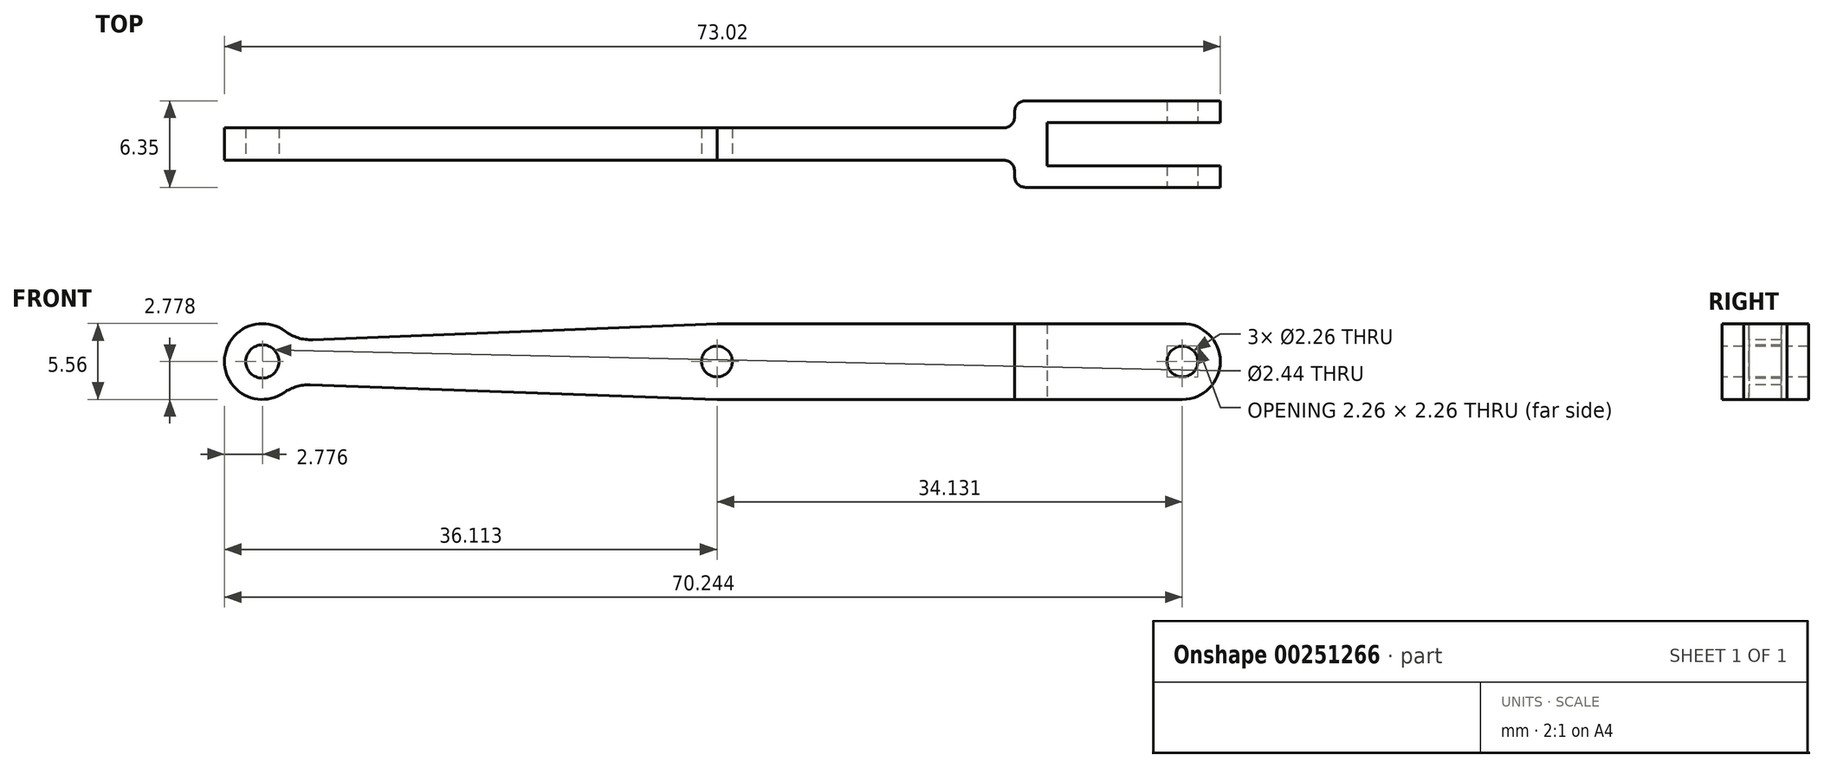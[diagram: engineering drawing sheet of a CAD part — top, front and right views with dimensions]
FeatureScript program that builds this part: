
annotation { "Feature Type Name" : "Feature", "Feature Type Description" : "" }
export const myFeature = defineFeature(function(context is Context, id is Id, definition is map)
    precondition{}
    {
        {
            var Q0;
            Q0=qCreatedBy(makeId("Top.planeOp"),FACE);
            var sketch = newSketch(context, id + "F0", { "sketchPlane" : qUnion([Q0])});
            skLineSegment(sketch, "E0", {"start": v(-28.05, 23.01) * mm, "end": v(29.1, 23.01) * mm});
            skLineSegment(sketch, "E1", {"start": v(29.9, 23.8) * mm, "end": v(29.9, 24.2) * mm});
            skLineSegment(sketch, "E2", {"start": v(30.68, 25) * mm, "end": v(44.97, 25) * mm});
            skLineSegment(sketch, "E3", {"start": v(44.97, 25) * mm, "end": v(44.97, 23.4) * mm});
            skLineSegment(sketch, "E4", {"start": v(44.97, 23.4) * mm, "end": v(32.27, 23.4) * mm});
            skLineSegment(sketch, "E5", {"start": v(32.27, 23.4) * mm, "end": v(32.27, 20.23) * mm});
            skLineSegment(sketch, "E6", {"start": v(32.27, 20.23) * mm, "end": v(44.97, 20.23) * mm});
            skLineSegment(sketch, "E7", {"start": v(44.97, 20.23) * mm, "end": v(44.97, 18.65) * mm});
            skLineSegment(sketch, "E8", {"start": v(44.97, 18.65) * mm, "end": v(30.68, 18.65) * mm});
            skLineSegment(sketch, "E9", {"start": v(29.9, 19.44) * mm, "end": v(29.9, 19.84) * mm});
            skLineSegment(sketch, "E10", {"start": v(29.1, 20.63) * mm, "end": v(-28.05, 20.63) * mm});
            skLineSegment(sketch, "E11", {"start": v(-28.05, 20.63) * mm, "end": v(-28.05, 23.01) * mm});
            skPoint(sketch, "E12.visualSharp", {"position": v(29.9, 23.01) * mm});
            skArc(sketch, "E12.filletArc", {"start": v(29.1, 23.01) * mm, "mid": v(29.66, 23.25) * mm, "end": v(29.9, 23.8) * mm});
            skPoint(sketch, "E13.visualSharp", {"position": v(29.9, 25) * mm});
            skArc(sketch, "E13.filletArc", {"start": v(30.68, 25) * mm, "mid": v(30.12, 24.76) * mm, "end": v(29.9, 24.2) * mm});
            skPoint(sketch, "E14.visualSharp", {"position": v(29.9, 20.63) * mm});
            skArc(sketch, "E14.filletArc", {"start": v(29.9, 19.84) * mm, "mid": v(29.66, 20.4) * mm, "end": v(29.1, 20.63) * mm});
            skPoint(sketch, "E15.visualSharp", {"position": v(29.9, 18.65) * mm});
            skArc(sketch, "E15.filletArc", {"start": v(29.9, 19.44) * mm, "mid": v(30.12, 18.88) * mm, "end": v(30.68, 18.65) * mm});
            skSolve(sketch);
        }
        {
            var Q0;
            Q0 = qSketchRegion(id + "F0", true);
            extrude(context, id + "F1", {"entities" : qUnion([Q0]), "depth" : 5.56 * mm});
        }
        {
            var Q0;
            Q0=makeQuery(id+"F1.opExtrude","SWEPT_FACE",FACE,{"disambiguationData":[OSD([sQuery(id+"F0.wireOp",EDGE,"E10")])]});
            var sketch = newSketch(context, id + "F2", { "sketchPlane" : qUnion([Q0])});
            skCircle(sketch, "E16", {"center": v(-25.27, 2.78) * mm, "radius": 1.22 * mm});
            skSolve(sketch);
        }
        {
            var Q0;
            Q0 = qSketchRegion(id + "F2", true);
            extrude(context, id + "F3", {"entities" : qUnion([Q0]), "operationType" : NewBodyOperationType.REMOVE, "oppositeDirection" : true, "depth" : 25.4 * mm});
        }
        {
            var Q0;
            Q0=makeQuery(id+"F1.opExtrude","SWEPT_FACE",FACE,{"disambiguationData":[OSD([sQuery(id+"F0.wireOp",EDGE,"E8")])]});
            var sketch = newSketch(context, id + "F4", { "sketchPlane" : qUnion([Q0])});
            skCircle(sketch, "E17", {"center": v(42.2, 2.78) * mm, "radius": 1.13 * mm});
            skSolve(sketch);
        }
        {
            var Q0;
            Q0 = qSketchRegion(id + "F4", true);
            extrude(context, id + "F5", {"entities" : qUnion([Q0]), "operationType" : NewBodyOperationType.REMOVE, "oppositeDirection" : true, "depth" : 25.4 * mm});
        }
        {
            var Q0;
            Q0=makeQuery(id+"F1.opExtrude","CAP_EDGE",EDGE,{"disambiguationData":[OSD([sQuery(id+"F0.wireOp",EDGE,"E7")])],"isStart":false});
            var Q1;
            Q1=makeQuery(id+"F1.opExtrude","CAP_EDGE",EDGE,{"disambiguationData":[OSD([sQuery(id+"F0.wireOp",EDGE,"E7")])],"isStart":true});
            var Q2;
            Q2=makeQuery(id+"F1.opExtrude","CAP_EDGE",EDGE,{"disambiguationData":[OSD([sQuery(id+"F0.wireOp",EDGE,"E3")])],"isStart":true});
            var Q3;
            Q3=makeQuery(id+"F1.opExtrude","CAP_EDGE",EDGE,{"disambiguationData":[OSD([sQuery(id+"F0.wireOp",EDGE,"E3")])],"isStart":false});
            fillet(context, id + "F6", {"entities" : qUnion([Q0, Q1, Q2, Q3]), "radius" : 2.78 * mm, "tangentPropagation" : true, "allowEdgeOverflow" : false});
        }
        {
            var Q0;
            Q0=makeQuery(id+"F1.opExtrude","CAP_EDGE",EDGE,{"disambiguationData":[OSD([sQuery(id+"F0.wireOp",EDGE,"E11")])],"isStart":false});
            var Q1;
            Q1=makeQuery(id+"F1.opExtrude","CAP_EDGE",EDGE,{"disambiguationData":[OSD([sQuery(id+"F0.wireOp",EDGE,"E11")])],"isStart":true});
            fillet(context, id + "F7", {"entities" : qUnion([Q0, Q1]), "radius" : 2.78 * mm, "tangentPropagation" : true, "allowEdgeOverflow" : false});
        }
        {
            var Q0;
            Q0=makeQuery(id+"F1.opExtrude","SWEPT_FACE",FACE,{"disambiguationData":[OSD([sQuery(id+"F0.wireOp",EDGE,"E10")])]});
            var sketch = newSketch(context, id + "F8", { "sketchPlane" : qUnion([Q0])});
            skCircle(sketch, "E18", {"center": v(8.06, 2.78) * mm, "radius": 1.13 * mm});
            skArc(sketch, "E19", {"start": v(-25.27, 0) * mm, "mid": v(-22.5, 2.78) * mm, "end": v(-25.27, 5.56) * mm});
            skPoint(sketch, "E20", {"position": v(8.06, 5.56) * mm});
            skPoint(sketch, "E21", {"position": v(8.06, 0) * mm});
            skLineSegment(sketch, "E22", {"start": v(-22.96, 4.32) * mm, "end": v(8.06, 5.56) * mm});
            skLineSegment(sketch, "E23", {"start": v(-23.05, 1.11) * mm, "end": v(8.06, 0) * mm});
            skArc(sketch, "E24", {"start": v(-23.61, 5) * mm, "mid": v(-22.65, 4.52) * mm, "end": v(-21.59, 4.38) * mm});
            skArc(sketch, "E25", {"start": v(-21.76, 1.07) * mm, "mid": v(-22.77, 0.94) * mm, "end": v(-23.69, 0.5) * mm});
            skSolve(sketch);
        }
        {
            var Q0;
            Q0=makeQuery(id+"F8.imprint","IMPRINT",FACE,{"disambiguationData":[TD([[makeQuery(id+"F8.imprint","IMPRINT",EDGE,{"derivedFrom":sQuery(id+"F8.wireOp",EDGE,"E18")}),1.0]])]});
            var Q1;
            {var subQ4=sQuery(id+"F8.wireOp",EDGE,"E24");Q1=makeQuery(id+"F8.imprint","IMPRINT",FACE,{"disambiguationData":[TD([[makeQuery(id+"F8.imprint","IMPRINT",EDGE,{"derivedFrom":subQ4}),1.0]])]});}
            var Q2;
            {var subQ4=sQuery(id+"F8.wireOp",EDGE,"E25");Q2=makeQuery(id+"F8.imprint","IMPRINT",FACE,{"disambiguationData":[TD([[makeQuery(id+"F8.imprint","IMPRINT",EDGE,{"derivedFrom":subQ4}),1.0]])]});}
            extrude(context, id + "F9", {"entities" : qUnion([Q0, Q1, Q2]), "operationType" : NewBodyOperationType.REMOVE, "oppositeDirection" : true, "depth" : 25.4 * mm});
        }
    });
